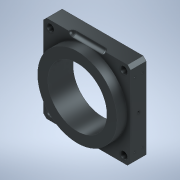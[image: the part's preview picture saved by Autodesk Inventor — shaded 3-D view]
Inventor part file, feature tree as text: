
AUTODESK INVENTOR PART (.ipt)
format: ipt  version: 2020 (Build 240168000, 168)  size: 250,880 bytes
history: native  units: mm
features: extrude x6, sketch x6, projected_geometry x6, revolve x1, thread x1, chamfer x1
ambient origin geometry x8: Origin, YZ Plane, XZ Plane, XY Plane, X Axis, Y Axis, Z Axis, Center Point
bodies: Solid1 (feature_tree)
feature tree (21):
  extrude  "Extrusion1"  Depth=71.1mm
  extrude  "Extrusion2"  Depth=12.7mm TaperAngle=0.0deg
  revolve  "Revolution1"  [1 undecoded]
  extrude  "Extrusion3"  Depth=15.0mm
  extrude  "Extrusion4"  Depth=3.15mm
  extrude  "Extrusion5"  TaperAngle=90.0deg  [1 undecoded]
  thread  "Thread1"  [1 undecoded]
  chamfer  "Chamfer1"  Distance=30.0mm
  extrude  "Extrusion6"  Depth=4.75mm
  sketch  "Sketch1"  dims[d0=71.1mm d1=71.1mm]
  sketch  "Sketch2"  dims[d2=48.3mm d3=12.7mm d4=0.0mm]
  projected_geometry  "Projected Loop1"
  sketch  "Sketch3"  dims[d5=64.8mm d6=7.9mm d7=0.0mm]
  projected_geometry  "Projected Loop2"
  sketch  "Sketch4"  dims[d8=35.55mm d9=15.0mm]
  projected_geometry  "Projected Loop3"
  projected_geometry  "Projected Loop4"
  sketch  "Sketch6"  dims[d10=3.15mm d11=11.85mm]
  projected_geometry  "Projected Loop5"
  sketch  "Sketch7"  dims[d12=6.3mm d13=90.0deg d14=30.0mm d15=30.0mm d16=60.0mm d17=60.0mm d18=60.0mm d19=6.0mm d20=6.0mm d21=6.0mm d22=6.0mm d23=12.7mm d24=0.0mm d25=6.35mm d26=2.0mm d27=4.75mm d28=0.0mm d29=4.0mm d30=6.1mm d31=0.0mm d32=6.1mm d33=0.0mm d34=2.55mm d35=2.0mm d36=45.0deg d37=3.175mm d38=30.0mm d39=3.58mm d40=6.35mm d41=60.0mm d42=3.58mm d43=6.35mm d44=1.3mm d45=1.3mm d46=1.3mm d47=1.3mm d48=6.35mm d49=1.3mm d50=1.3mm d51=2.0mm d52=1.3mm d53=1.3mm d54=4.75mm d55=0.0mm]
  projected_geometry  "Projected Loop6"
note: 3 required parameter values undecoded (feature->parameter linkage not recoverable at this tier; creation-order binding heuristic only, values carry confidence <= 0.55)